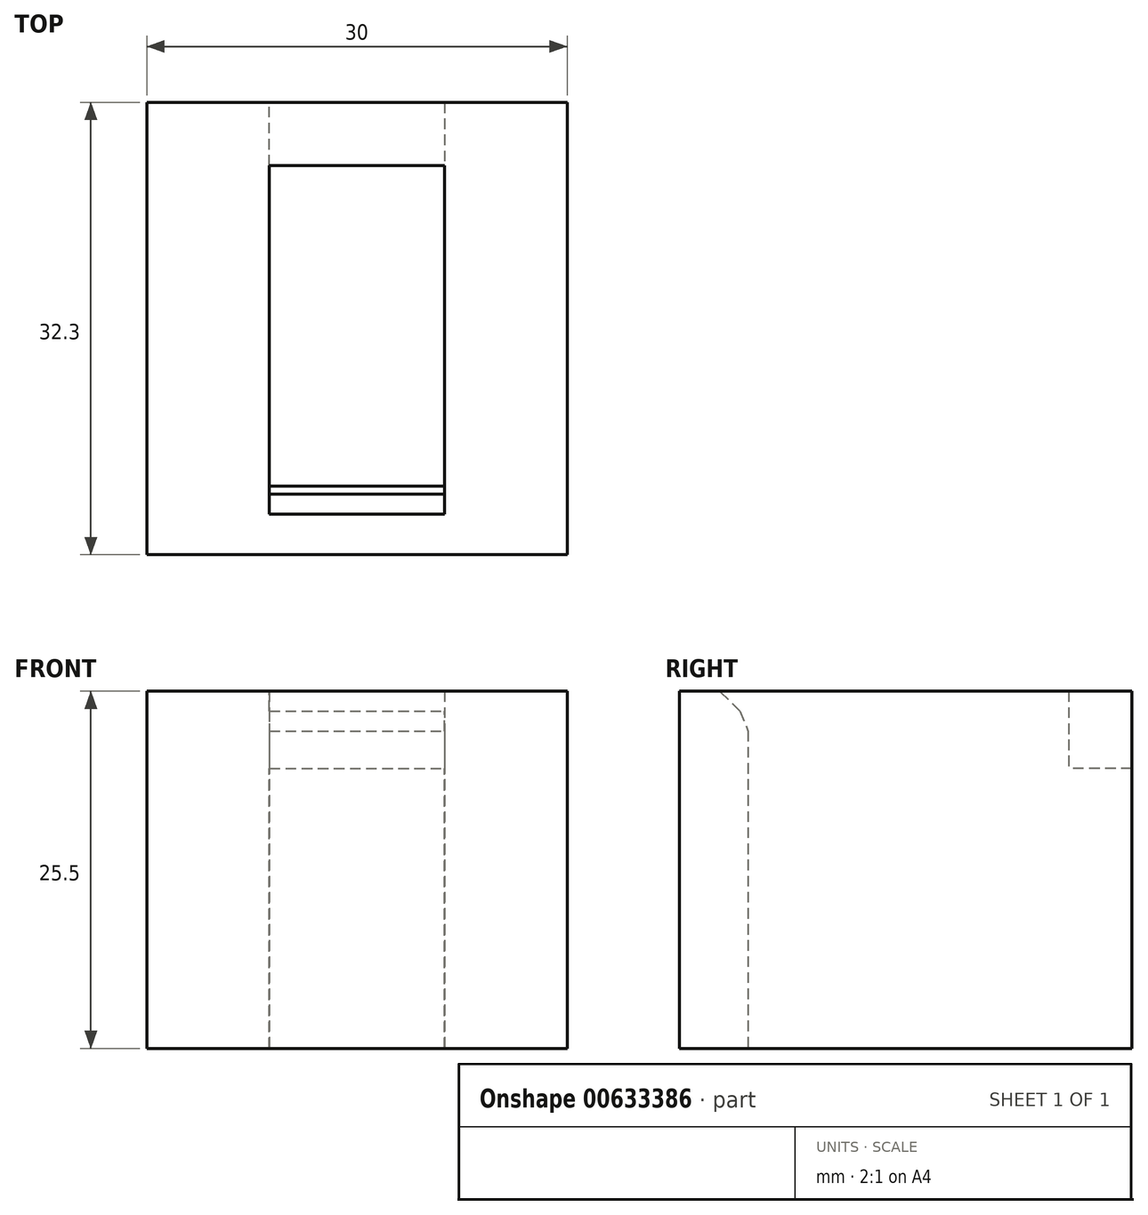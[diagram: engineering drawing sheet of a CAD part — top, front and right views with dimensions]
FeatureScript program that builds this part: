
annotation { "Feature Type Name" : "Feature", "Feature Type Description" : "" }
export const myFeature = defineFeature(function(context is Context, id is Id, definition is map)
    precondition{}
    {
        {
            var Q0;
            Q0=qCreatedBy(makeId("Top.planeOp"),FACE);
            var sketch = newSketch(context, id + "F0", { "sketchPlane" : qUnion([Q0])});
            skLineSegment(sketch, "E0.bottom", {"start": v(0, 0) * mm, "end": v(12.5, 0) * mm});
            skLineSegment(sketch, "E0.top", {"start": v(0, 22.9) * mm, "end": v(12.5, 22.9) * mm});
            skLineSegment(sketch, "E0.left", {"start": v(0, 0) * mm, "end": v(0, 22.9) * mm});
            skLineSegment(sketch, "E0.right", {"start": v(12.5, 0) * mm, "end": v(12.5, 22.9) * mm});
            skSolve(sketch);
        }
        {
            var Q0;
            Q0=qCreatedBy(makeId("Top.planeOp"),FACE);
            var sketch = newSketch(context, id + "F1", { "sketchPlane" : qUnion([Q0])});
            skLineSegment(sketch, "E1", {"start": v(-8.75, -4.9) * mm, "end": v(-8.75, 27.4) * mm});
            skLineSegment(sketch, "E2", {"start": v(-8.75, 27.4) * mm, "end": v(21.25, 27.4) * mm});
            skLineSegment(sketch, "E3", {"start": v(21.25, 27.4) * mm, "end": v(21.25, -4.9) * mm});
            skLineSegment(sketch, "E4", {"start": v(21.25, -4.9) * mm, "end": v(-8.75, -4.9) * mm});
            skSolve(sketch);
        }
        {
            var Q0;
            Q0=qSketchRegion(id+"F1",true);
            extrude(context, id + "F2", {"entities" : qUnion([Q0]), "depth" : 5.5 * mm, "offsetDistance" : 25 * mm});
        }
        {
            var Q0;
            Q0=qSketchRegion(id+"F0",true);
            extrude(context, id + "F3", {"entities" : qUnion([Q0]), "operationType" : NewBodyOperationType.REMOVE, "depth" : 7 * mm, "offsetDistance" : 25 * mm});
        }
        {
            var Q0;
            Q0=qCreatedBy(makeId("Top.planeOp"),FACE);
            var sketch = newSketch(context, id + "F4", { "sketchPlane" : qUnion([Q0])});
            skPoint(sketch, "E5", {"position": v(12.5, 0) * mm});
            skPoint(sketch, "E6", {"position": v(0, 22.9) * mm});
            skPoint(sketch, "E7", {"position": v(12.5, 22.9) * mm});
            skPoint(sketch, "E8", {"position": v(-8.75, -4.9) * mm});
            skPoint(sketch, "E9", {"position": v(21.25, -4.9) * mm});
            skPoint(sketch, "E10", {"position": v(21.25, 27.4) * mm});
            skPoint(sketch, "E11", {"position": v(-8.75, 27.4) * mm});
            skLineSegment(sketch, "E12.bottom", {"start": v(0, 0) * mm, "end": v(-8.75, 0) * mm});
            skLineSegment(sketch, "E12.top", {"start": v(0, -4.9) * mm, "end": v(-8.75, -4.9) * mm});
            skLineSegment(sketch, "E12.left", {"start": v(0, 0) * mm, "end": v(0, -4.9) * mm});
            skLineSegment(sketch, "E12.right", {"start": v(-8.75, 0) * mm, "end": v(-8.75, -4.9) * mm});
            skLineSegment(sketch, "E13.bottom", {"start": v(12.5, 0) * mm, "end": v(21.25, 0) * mm});
            skLineSegment(sketch, "E13.top", {"start": v(12.5, -4.9) * mm, "end": v(21.25, -4.9) * mm});
            skLineSegment(sketch, "E13.left", {"start": v(12.5, 0) * mm, "end": v(12.5, -4.9) * mm});
            skLineSegment(sketch, "E13.right", {"start": v(21.25, 0) * mm, "end": v(21.25, -4.9) * mm});
            skLineSegment(sketch, "E14.bottom", {"start": v(21.25, 27.4) * mm, "end": v(12.5, 27.4) * mm});
            skLineSegment(sketch, "E14.top", {"start": v(21.25, 22.9) * mm, "end": v(12.5, 22.9) * mm});
            skLineSegment(sketch, "E14.left", {"start": v(21.25, 27.4) * mm, "end": v(21.25, 22.9) * mm});
            skLineSegment(sketch, "E14.right", {"start": v(12.5, 27.4) * mm, "end": v(12.5, 22.9) * mm});
            skLineSegment(sketch, "E15.bottom", {"start": v(0, 22.9) * mm, "end": v(-8.75, 22.9) * mm});
            skLineSegment(sketch, "E15.top", {"start": v(0, 27.4) * mm, "end": v(-8.75, 27.4) * mm});
            skLineSegment(sketch, "E15.left", {"start": v(0, 22.9) * mm, "end": v(0, 27.4) * mm});
            skLineSegment(sketch, "E15.right", {"start": v(-8.75, 22.9) * mm, "end": v(-8.75, 27.4) * mm});
            skLineSegment(sketch, "E16.left", {"start": v(0, 0) * mm, "end": v(0, 22.9) * mm});
            skLineSegment(sketch, "E16.right", {"start": v(-8.75, 0) * mm, "end": v(-8.75, 22.9) * mm});
            skLineSegment(sketch, "E17.bottom", {"start": v(0, 0) * mm, "end": v(12.5, 0) * mm});
            skLineSegment(sketch, "E17.top", {"start": v(0, -4.9) * mm, "end": v(12.5, -4.9) * mm});
            skLineSegment(sketch, "E18.bottom", {"start": v(21.25, 0) * mm, "end": v(12.5, 0) * mm});
            skLineSegment(sketch, "E18.left", {"start": v(21.25, 0) * mm, "end": v(21.25, 22.9) * mm});
            skLineSegment(sketch, "E18.right", {"start": v(12.5, 0) * mm, "end": v(12.5, 22.9) * mm});
            skSolve(sketch);
        }
        {
            var Q0;
            Q0=qSketchRegion(id+"F4",true);
            extrude(context, id + "F5", {"entities" : qUnion([Q0]), "operationType" : NewBodyOperationType.ADD, "oppositeDirection" : true, "depth" : 20 * mm, "offsetDistance" : 25 * mm});
        }
        {
            var Q0;
            Q0=makeQuery(id+"F3.boolean.opBoolean","INTERSECT",EDGE,{"derivedFrom":[makeQuery(id+"F2.opExtrude","CAP_FACE",FACE,{"disambiguationData":[OSD([sQuery(id+"F1.wireOp",EDGE,"E1"),sQuery(id+"F1.wireOp",EDGE,"E2"),sQuery(id+"F1.wireOp",EDGE,"E3"),sQuery(id+"F1.wireOp",EDGE,"E4")])],"isStart":false}),makeQuery(id+"F3.opExtrude","SWEPT_FACE",FACE,{"disambiguationData":[OSD([sQuery(id+"F0.wireOp",EDGE,"E0.bottom")])]})]});
            chamfer(context, id + "F6", {"entities" : qUnion([Q0]), "width" : 2 * mm, "tangentPropagation" : true});
        }
        {
            var Q0;
            {var subQ0=makeQuery(id+"F3.opExtrude","SWEPT_FACE",FACE,{"disambiguationData":[OSD([sQuery(id+"F0.wireOp",EDGE,"E0.bottom")])]});Q0=makeQuery(id+"F6.opChamfer","BLEND_EDGE",EDGE,{"blendedFrom":[makeQuery(id+"F3.boolean.opBoolean","INTERSECT",EDGE,{"derivedFrom":[makeQuery(id+"F2.opExtrude","CAP_FACE",FACE,{"disambiguationData":[OSD([sQuery(id+"F1.wireOp",EDGE,"E1"),sQuery(id+"F1.wireOp",EDGE,"E2"),sQuery(id+"F1.wireOp",EDGE,"E3"),sQuery(id+"F1.wireOp",EDGE,"E4")])],"isStart":false}),subQ0]}),makeQuery(id+"F5.boolean.opBoolean","MERGE",FACE,{"derivedFrom":[makeQuery(id+"F3.boolean.opBoolean","COPY",FACE,{"derivedFrom":subQ0}),makeQuery(id+"F5.opExtrude","SWEPT_FACE",FACE,{"disambiguationData":[OSD([sQuery(id+"F4.wireOp",EDGE,"E17.bottom")])]})]})],"blendedInto":[makeQuery(id+"F5.boolean.opBoolean","MERGE",FACE,{"derivedFrom":[makeQuery(id+"F3.boolean.opBoolean","COPY",FACE,{"derivedFrom":subQ0}),makeQuery(id+"F5.opExtrude","SWEPT_FACE",FACE,{"disambiguationData":[OSD([sQuery(id+"F4.wireOp",EDGE,"E17.bottom")])]})]})]});}
            chamfer(context, id + "F7", {"entities" : qUnion([Q0]), "width" : 2 * mm, "tangentPropagation" : true});
        }
    });
